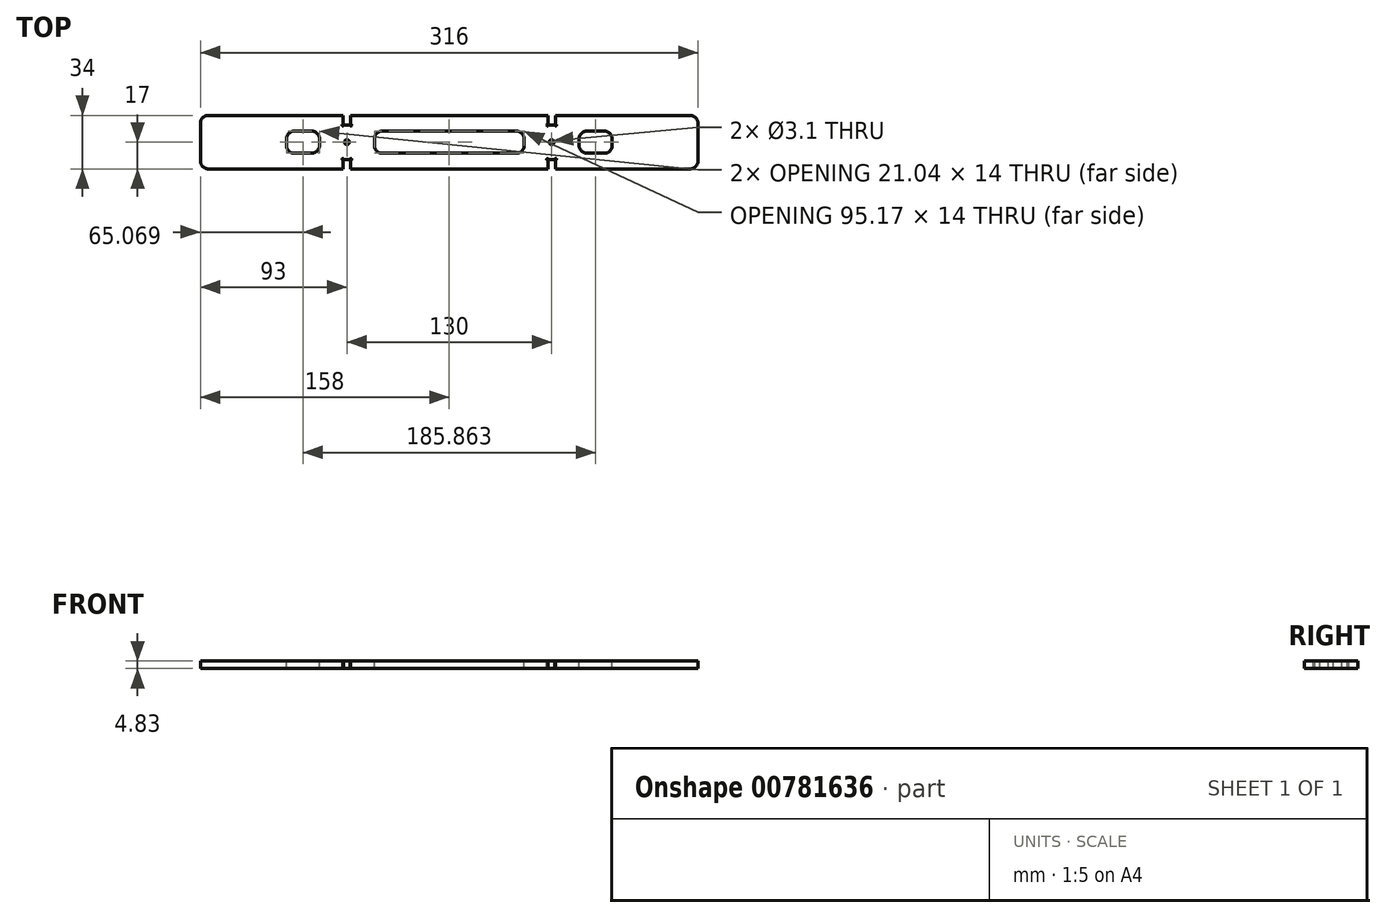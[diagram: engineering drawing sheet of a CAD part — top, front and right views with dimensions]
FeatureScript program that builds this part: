
annotation { "Feature Type Name" : "Feature", "Feature Type Description" : "" }
export const myFeature = defineFeature(function(context is Context, id is Id, definition is map)
    precondition{}
    {
        {
            var Q0;
            Q0=qCreatedBy(makeId("Top.planeOp"),FACE);
            var sketch = newSketch(context, id + "F0", { "sketchPlane" : qUnion([Q0])});
            skLineSegment(sketch, "E0.bottom", {"start": v(158, -17) * mm, "end": v(-158, -17) * mm});
            skLineSegment(sketch, "E0.top", {"start": v(158, 17) * mm, "end": v(-158, 17) * mm});
            skLineSegment(sketch, "E0.left", {"start": v(158, -17) * mm, "end": v(158, 17) * mm});
            skLineSegment(sketch, "E0.right", {"start": v(-158, -17) * mm, "end": v(-158, 17) * mm});
            skPoint(sketch, "E0.middle", {"position": v(0, 0) * mm});
            skSolve(sketch);
        }
        {
            var Q0;
            Q0=qSketchRegion(id+"F0",true);
            extrude(context, id + "F1", {"entities" : qUnion([Q0]), "depth" : 4.83 * mm, "offsetDistance" : 25 * mm});
        }
        {
            var Q0;
            Q0=makeQuery(id+"F1.opExtrude","CAP_FACE",FACE,{"disambiguationData":[OSD([sQuery(id+"F0.wireOp",EDGE,"E0.bottom"),sQuery(id+"F0.wireOp",EDGE,"E0.top"),sQuery(id+"F0.wireOp",EDGE,"E0.left"),sQuery(id+"F0.wireOp",EDGE,"E0.right")])],"isStart":false});
            var sketch = newSketch(context, id + "F2", { "sketchPlane" : qUnion([Q0])});
            skLineSegment(sketch, "E1.MirrorCS", {"start": v(-62.59, 17) * mm, "end": v(-62.59, 11) * mm});
            skLineSegment(sketch, "E2.MirrorCS", {"start": v(-67.41, 17) * mm, "end": v(-67.41, 11) * mm});
            skLineSegment(sketch, "E3.MirrorCS", {"start": v(-67.41, 11) * mm, "end": v(-62.59, 11) * mm});
            skLineSegment(sketch, "E4.MirrorCS", {"start": v(-67.41, 17) * mm, "end": v(-62.59, 17) * mm});
            skCircle(sketch, "E5", {"center": v(-65, 0) * mm, "radius": 1.55 * mm});
            skLineSegment(sketch, "E6", {"start": v(0, 17) * mm, "end": v(0, -17) * mm, "construction": true});
            skLineSegment(sketch, "E7", {"start": v(-65, 11) * mm, "end": v(-65, -11) * mm, "construction": true});
            skLineSegment(sketch, "E8.bottom", {"start": v(-67.41, -17) * mm, "end": v(-62.59, -17) * mm});
            skLineSegment(sketch, "E8.top", {"start": v(-67.41, -11) * mm, "end": v(-62.59, -11) * mm});
            skLineSegment(sketch, "E8.left", {"start": v(-67.41, -17) * mm, "end": v(-67.41, -11) * mm});
            skLineSegment(sketch, "E8.right", {"start": v(-62.59, -17) * mm, "end": v(-62.59, -11) * mm});
            skLineSegment(sketch, "E9.MirrorCS", {"start": v(-62.59, 11) * mm, "end": v(-67.41, 11) * mm});
            skLineSegment(sketch, "E10.MirrorCS", {"start": v(-62.59, 17) * mm, "end": v(-67.41, 17) * mm});
            skLineSegment(sketch, "E11.MirrorCS", {"start": v(-62.59, -11) * mm, "end": v(-67.41, -11) * mm});
            skLineSegment(sketch, "E12.MirrorCS", {"start": v(-62.59, -17) * mm, "end": v(-67.41, -17) * mm});
            skLineSegment(sketch, "E13.MirrorCS", {"start": v(62.59, -17) * mm, "end": v(62.59, -11) * mm});
            skLineSegment(sketch, "E14.MirrorCS", {"start": v(67.41, -17) * mm, "end": v(67.41, -11) * mm});
            skLineSegment(sketch, "E15.MirrorCS", {"start": v(67.41, -11) * mm, "end": v(62.59, -11) * mm});
            skLineSegment(sketch, "E16.MirrorCS", {"start": v(67.41, 17) * mm, "end": v(67.41, 11) * mm});
            skCircle(sketch, "E17.MirrorC", {"center": v(65, 0) * mm, "radius": 1.55 * mm});
            skLineSegment(sketch, "E18.MirrorCS", {"start": v(62.59, 17) * mm, "end": v(67.41, 17) * mm});
            skLineSegment(sketch, "E19.MirrorCS", {"start": v(67.41, -17) * mm, "end": v(62.59, -17) * mm});
            skLineSegment(sketch, "E20.MirrorCS", {"start": v(62.59, 17) * mm, "end": v(62.59, 11) * mm});
            skLineSegment(sketch, "E21.MirrorCS", {"start": v(62.59, 11) * mm, "end": v(67.41, 11) * mm});
            skLineSegment(sketch, "E22.MirrorCS", {"start": v(67.41, 11) * mm, "end": v(62.59, 11) * mm});
            skLineSegment(sketch, "E23.MirrorCS", {"start": v(62.59, -11) * mm, "end": v(67.41, -11) * mm});
            skLineSegment(sketch, "E24.MirrorCS", {"start": v(65, 11) * mm, "end": v(65, -11) * mm, "construction": true});
            skLineSegment(sketch, "E25.MirrorCS", {"start": v(62.59, -17) * mm, "end": v(67.41, -17) * mm});
            skLineSegment(sketch, "E26.MirrorCS", {"start": v(67.41, 17) * mm, "end": v(62.59, 17) * mm});
            skSolve(sketch);
        }
        {
            var Q0;
            Q0=qSketchRegion(id+"F2",true);
            var Q1;
            Q1=makeQuery(id+"F1.opExtrude","CAP_FACE",FACE,{"disambiguationData":[OSD([sQuery(id+"F0.wireOp",EDGE,"E0.bottom"),sQuery(id+"F0.wireOp",EDGE,"E0.top"),sQuery(id+"F0.wireOp",EDGE,"E0.left"),sQuery(id+"F0.wireOp",EDGE,"E0.right")])],"isStart":true});
            extrude(context, id + "F3", {"entities" : qUnion([Q0]), "operationType" : NewBodyOperationType.REMOVE, "endBound" : BoundingType.UP_TO_SURFACE, "oppositeDirection" : true, "depth" : 25 * mm, "endBoundEntityFace" : qUnion([Q1]), "offsetDistance" : 25 * mm});
        }
        {
            var Q0;
            Q0=makeQuery(id+"F1.opExtrude","CAP_FACE",FACE,{"disambiguationData":[OSD([sQuery(id+"F0.wireOp",EDGE,"E0.bottom"),sQuery(id+"F0.wireOp",EDGE,"E0.top"),sQuery(id+"F0.wireOp",EDGE,"E0.left"),sQuery(id+"F0.wireOp",EDGE,"E0.right")])],"isStart":false});
            var sketch = newSketch(context, id + "F4", { "sketchPlane" : qUnion([Q0])});
            skLineSegment(sketch, "E27", {"start": v(0, 17) * mm, "end": v(0, -17) * mm, "construction": true});
            skLineSegment(sketch, "E28", {"start": v(-158, 0) * mm, "end": v(158, 0) * mm, "construction": true});
            skLineSegment(sketch, "E29", {"start": v(-65, 11) * mm, "end": v(-65, -11) * mm, "construction": true});
            skLineSegment(sketch, "E30", {"start": v(-67.41, 11) * mm, "end": v(-67.59, 10.82) * mm, "construction": true});
            skCircle(sketch, "E31", {"center": v(-67.59, 10.82) * mm, "radius": 0.5 * mm});
            skCircle(sketch, "E32.MirrorC", {"center": v(-62.41, 10.82) * mm, "radius": 0.5 * mm});
            skLineSegment(sketch, "E33.MirrorCS", {"start": v(-67.41, -11) * mm, "end": v(-67.59, -10.82) * mm, "construction": true});
            skCircle(sketch, "E34.MirrorC", {"center": v(-67.59, -10.82) * mm, "radius": 0.5 * mm});
            skCircle(sketch, "E35.MirrorC", {"center": v(-62.41, -10.82) * mm, "radius": 0.5 * mm});
            skLineSegment(sketch, "E36.MirrorCS", {"start": v(67.41, 11) * mm, "end": v(67.59, 10.82) * mm, "construction": true});
            skLineSegment(sketch, "E37.MirrorCS", {"start": v(67.41, -11) * mm, "end": v(67.59, -10.82) * mm, "construction": true});
            skCircle(sketch, "E38.MirrorC", {"center": v(67.59, 10.82) * mm, "radius": 0.5 * mm});
            skCircle(sketch, "E39.MirrorC", {"center": v(67.59, -10.82) * mm, "radius": 0.5 * mm});
            skLineSegment(sketch, "E40.MirrorCS", {"start": v(65, 11) * mm, "end": v(65, -11) * mm, "construction": true});
            skCircle(sketch, "E41.MirrorC", {"center": v(62.41, -10.82) * mm, "radius": 0.5 * mm});
            skCircle(sketch, "E42.MirrorC", {"center": v(62.41, 10.82) * mm, "radius": 0.5 * mm});
            skSolve(sketch);
        }
        {
            var Q0;
            Q0 = qSketchRegion(id + "F4", true);
            extrude(context, id + "F5", {"entities" : qUnion([Q0]), "operationType" : NewBodyOperationType.REMOVE, "endBound" : BoundingType.THROUGH_ALL, "oppositeDirection" : true, "depth" : 25 * mm, "offsetDistance" : 25 * mm});
        }
        {
            var Q0;
            Q0=makeQuery(id+"F1.opExtrude","CAP_FACE",FACE,{"disambiguationData":[OSD([sQuery(id+"F0.wireOp",EDGE,"E0.bottom"),sQuery(id+"F0.wireOp",EDGE,"E0.top"),sQuery(id+"F0.wireOp",EDGE,"E0.left"),sQuery(id+"F0.wireOp",EDGE,"E0.right")])],"isStart":false});
            var sketch = newSketch(context, id + "F6", { "sketchPlane" : qUnion([Q0])});
            skCircle(sketch, "E43", {"center": v(-151.5, -7) * mm, "radius": 2.05 * mm});
            skCircle(sketch, "E44", {"center": v(-115.5, -7) * mm, "radius": 2.05 * mm});
            skLineSegment(sketch, "E45", {"start": v(-115.5, -7) * mm, "end": v(-151.5, -7) * mm, "construction": true});
            skLineSegment(sketch, "E46.bottom", {"start": v(-158, -10) * mm, "end": v(-109, -10) * mm, "construction": true});
            skLineSegment(sketch, "E46.top", {"start": v(-158, 69) * mm, "end": v(-109, 69) * mm, "construction": true});
            skLineSegment(sketch, "E46.left", {"start": v(-158, -10) * mm, "end": v(-158, 69) * mm, "construction": true});
            skLineSegment(sketch, "E46.right", {"start": v(-109, -10) * mm, "end": v(-109, 69) * mm, "construction": true});
            skLineSegment(sketch, "E47", {"start": v(-133.5, -10) * mm, "end": v(-133.5, 69) * mm, "construction": true});
            skLineSegment(sketch, "E48", {"start": v(-109, 29.5) * mm, "end": v(-158, 29.5) * mm, "construction": true});
            skPoint(sketch, "E49", {"position": v(-133.5, -7) * mm});
            skCircle(sketch, "E50", {"center": v(-151.5, -7) * mm, "radius": 6.25 * mm, "construction": true});
            skSolve(sketch);
        }
        {
            var Q0;
            Q0=makeQuery(id+"F1.opExtrude","CAP_FACE",FACE,{"disambiguationData":[OSD([sQuery(id+"F0.wireOp",EDGE,"E0.bottom"),sQuery(id+"F0.wireOp",EDGE,"E0.top"),sQuery(id+"F0.wireOp",EDGE,"E0.left"),sQuery(id+"F0.wireOp",EDGE,"E0.right")])],"isStart":false});
            var sketch = newSketch(context, id + "F7", { "sketchPlane" : qUnion([Q0])});
            skCircle(sketch, "E51", {"center": v(112.5, -6) * mm, "radius": 2.05 * mm});
            skCircle(sketch, "E52", {"center": v(148.5, -6) * mm, "radius": 2.05 * mm});
            skLineSegment(sketch, "E53", {"start": v(148.5, -6) * mm, "end": v(112.5, -6) * mm, "construction": true});
            skLineSegment(sketch, "E54.bottom", {"start": v(103, -10) * mm, "end": v(158, -10) * mm, "construction": true});
            skLineSegment(sketch, "E54.top", {"start": v(103, 71.7) * mm, "end": v(158, 71.7) * mm, "construction": true});
            skLineSegment(sketch, "E54.left", {"start": v(103, -10) * mm, "end": v(103, 71.7) * mm, "construction": true});
            skLineSegment(sketch, "E54.right", {"start": v(158, -10) * mm, "end": v(158, 71.7) * mm, "construction": true});
            skLineSegment(sketch, "E55", {"start": v(130.5, -10) * mm, "end": v(130.5, 71.7) * mm, "construction": true});
            skLineSegment(sketch, "E56", {"start": v(158, 30.85) * mm, "end": v(103, 30.85) * mm, "construction": true});
            skPoint(sketch, "E57", {"position": v(130.5, -6) * mm});
            skCircle(sketch, "E58", {"center": v(112.5, 3.4) * mm, "radius": 2.05 * mm});
            skCircle(sketch, "E59", {"center": v(148.5, 3.4) * mm, "radius": 2.05 * mm});
            skLineSegment(sketch, "E60", {"start": v(112.5, -6) * mm, "end": v(112.5, 3.4) * mm, "construction": true});
            skLineSegment(sketch, "E61", {"start": v(148.5, 3.4) * mm, "end": v(148.5, -6) * mm, "construction": true});
            skSolve(sketch);
        }
        {
            var Q0;
            Q0=makeQuery(id+"F1.opExtrude","CAP_FACE",FACE,{"disambiguationData":[OSD([sQuery(id+"F0.wireOp",EDGE,"E0.bottom"),sQuery(id+"F0.wireOp",EDGE,"E0.top"),sQuery(id+"F0.wireOp",EDGE,"E0.left"),sQuery(id+"F0.wireOp",EDGE,"E0.right")])],"isStart":false});
            var sketch = newSketch(context, id + "F9", { "sketchPlane" : qUnion([Q0])});
            skLineSegment(sketch, "E62.bottom", {"start": v(47.59, -7) * mm, "end": v(-47.59, -7) * mm});
            skLineSegment(sketch, "E62.top", {"start": v(47.59, 7) * mm, "end": v(-47.59, 7) * mm});
            skLineSegment(sketch, "E62.left", {"start": v(47.59, -7) * mm, "end": v(47.59, 7) * mm});
            skLineSegment(sketch, "E62.right", {"start": v(-47.59, -7) * mm, "end": v(-47.59, 7) * mm});
            skPoint(sketch, "E62.middle", {"position": v(0, 0) * mm});
            skLineSegment(sketch, "E63", {"start": v(0, -17) * mm, "end": v(0, 17) * mm, "construction": true});
            skLineSegment(sketch, "E64.bottom", {"start": v(-82.41, -7) * mm, "end": v(-103.45, -7) * mm});
            skLineSegment(sketch, "E64.top", {"start": v(-82.41, 7) * mm, "end": v(-103.45, 7) * mm});
            skLineSegment(sketch, "E64.left", {"start": v(-82.41, -7) * mm, "end": v(-82.41, 7) * mm});
            skLineSegment(sketch, "E64.right", {"start": v(-103.45, -7) * mm, "end": v(-103.45, 7) * mm});
            skPoint(sketch, "E64.middle", {"position": v(-92.93, 0) * mm});
            skLineSegment(sketch, "E65.MirrorCS", {"start": v(82.41, 7) * mm, "end": v(103.45, 7) * mm});
            skLineSegment(sketch, "E66.MirrorCS", {"start": v(103.45, -7) * mm, "end": v(103.45, 7) * mm});
            skLineSegment(sketch, "E67.MirrorCS", {"start": v(82.41, -7) * mm, "end": v(82.41, 7) * mm});
            skPoint(sketch, "E68.MirrorP", {"position": v(92.93, 0) * mm});
            skLineSegment(sketch, "E69.MirrorCS", {"start": v(82.41, -7) * mm, "end": v(103.45, -7) * mm});
            skSolve(sketch);
        }
        {
            var Q0;
            Q0 = qSketchRegion(id + "F9", true);
            extrude(context, id + "F10", {"entities" : qUnion([Q0]), "operationType" : NewBodyOperationType.REMOVE, "endBound" : BoundingType.THROUGH_ALL, "oppositeDirection" : true, "depth" : 25 * mm, "offsetDistance" : 25 * mm});
        }
        {
            var Q0;
            Q0=makeQuery(id+"F10.boolean.opBoolean","COPY",EDGE,{"derivedFrom":makeQuery(id+"F10.opExtrude","SWEPT_EDGE",EDGE,{"disambiguationData":[OSD([sQuery(id+"F9.wireOp",EDGE,"E64.bottom"),sQuery(id+"F9.wireOp",EDGE,"E64.right")])]})});
            var Q1;
            Q1=makeQuery(id+"F10.boolean.opBoolean","COPY",EDGE,{"derivedFrom":makeQuery(id+"F10.opExtrude","SWEPT_EDGE",EDGE,{"disambiguationData":[OSD([sQuery(id+"F9.wireOp",EDGE,"E64.top"),sQuery(id+"F9.wireOp",EDGE,"E64.right")])]})});
            var Q2;
            Q2=makeQuery(id+"F10.boolean.opBoolean","COPY",EDGE,{"derivedFrom":makeQuery(id+"F10.opExtrude","SWEPT_EDGE",EDGE,{"disambiguationData":[OSD([sQuery(id+"F9.wireOp",EDGE,"E64.top"),sQuery(id+"F9.wireOp",EDGE,"E64.left")])]})});
            var Q3;
            Q3=makeQuery(id+"F10.boolean.opBoolean","COPY",EDGE,{"derivedFrom":makeQuery(id+"F10.opExtrude","SWEPT_EDGE",EDGE,{"disambiguationData":[OSD([sQuery(id+"F9.wireOp",EDGE,"E64.bottom"),sQuery(id+"F9.wireOp",EDGE,"E64.left")])]})});
            var Q4;
            Q4=makeQuery(id+"F10.boolean.opBoolean","COPY",EDGE,{"derivedFrom":makeQuery(id+"F10.opExtrude","SWEPT_EDGE",EDGE,{"disambiguationData":[OSD([sQuery(id+"F9.wireOp",EDGE,"E62.bottom"),sQuery(id+"F9.wireOp",EDGE,"E62.right")])]})});
            var Q5;
            Q5=makeQuery(id+"F10.boolean.opBoolean","COPY",EDGE,{"derivedFrom":makeQuery(id+"F10.opExtrude","SWEPT_EDGE",EDGE,{"disambiguationData":[OSD([sQuery(id+"F9.wireOp",EDGE,"E62.top"),sQuery(id+"F9.wireOp",EDGE,"E62.right")])]})});
            var Q6;
            Q6=makeQuery(id+"F10.boolean.opBoolean","COPY",EDGE,{"derivedFrom":makeQuery(id+"F10.opExtrude","SWEPT_EDGE",EDGE,{"disambiguationData":[OSD([sQuery(id+"F9.wireOp",EDGE,"E62.bottom"),sQuery(id+"F9.wireOp",EDGE,"E62.left")])]})});
            var Q7;
            Q7=makeQuery(id+"F10.boolean.opBoolean","COPY",EDGE,{"derivedFrom":makeQuery(id+"F10.opExtrude","SWEPT_EDGE",EDGE,{"disambiguationData":[OSD([sQuery(id+"F9.wireOp",EDGE,"E62.top"),sQuery(id+"F9.wireOp",EDGE,"E62.left")])]})});
            var Q8;
            Q8=makeQuery(id+"F10.boolean.opBoolean","COPY",EDGE,{"derivedFrom":makeQuery(id+"F10.opExtrude","SWEPT_EDGE",EDGE,{"disambiguationData":[OSD([sQuery(id+"F9.wireOp",EDGE,"E65.MirrorCS"),sQuery(id+"F9.wireOp",EDGE,"E66.MirrorCS")])]})});
            var Q9;
            Q9=makeQuery(id+"F10.boolean.opBoolean","COPY",EDGE,{"derivedFrom":makeQuery(id+"F10.opExtrude","SWEPT_EDGE",EDGE,{"disambiguationData":[OSD([sQuery(id+"F9.wireOp",EDGE,"E66.MirrorCS"),sQuery(id+"F9.wireOp",EDGE,"E69.MirrorCS")])]})});
            var Q10;
            Q10=makeQuery(id+"F10.boolean.opBoolean","COPY",EDGE,{"derivedFrom":makeQuery(id+"F10.opExtrude","SWEPT_EDGE",EDGE,{"disambiguationData":[OSD([sQuery(id+"F9.wireOp",EDGE,"E67.MirrorCS"),sQuery(id+"F9.wireOp",EDGE,"E69.MirrorCS")])]})});
            var Q11;
            Q11=makeQuery(id+"F10.boolean.opBoolean","COPY",EDGE,{"derivedFrom":makeQuery(id+"F10.opExtrude","SWEPT_EDGE",EDGE,{"disambiguationData":[OSD([sQuery(id+"F9.wireOp",EDGE,"E65.MirrorCS"),sQuery(id+"F9.wireOp",EDGE,"E67.MirrorCS")])]})});
            fillet(context, id + "F11", {"entities" : qUnion([Q0, Q1, Q2, Q3, Q4, Q5, Q6, Q7, Q8, Q9, Q10, Q11]), "radius" : 5 * mm, "tangentPropagation" : true, "allowEdgeOverflow" : false});
        }
        {
            var Q0;
            Q0=makeQuery(id+"F1.opExtrude","SWEPT_EDGE",EDGE,{"disambiguationData":[OSD([sQuery(id+"F0.wireOp",EDGE,"E0.top"),sQuery(id+"F0.wireOp",EDGE,"E0.right")])]});
            var Q1;
            Q1=makeQuery(id+"F1.opExtrude","SWEPT_EDGE",EDGE,{"disambiguationData":[OSD([sQuery(id+"F0.wireOp",EDGE,"E0.bottom"),sQuery(id+"F0.wireOp",EDGE,"E0.right")])]});
            var Q2;
            Q2=makeQuery(id+"F1.opExtrude","SWEPT_EDGE",EDGE,{"disambiguationData":[OSD([sQuery(id+"F0.wireOp",EDGE,"E0.top"),sQuery(id+"F0.wireOp",EDGE,"E0.left")])]});
            var Q3;
            Q3=makeQuery(id+"F1.opExtrude","SWEPT_EDGE",EDGE,{"disambiguationData":[OSD([sQuery(id+"F0.wireOp",EDGE,"E0.bottom"),sQuery(id+"F0.wireOp",EDGE,"E0.left")])]});
            fillet(context, id + "F12", {"entities" : qUnion([Q0, Q1, Q2, Q3]), "radius" : 5 * mm, "tangentPropagation" : true, "allowEdgeOverflow" : false});
        }
    });
